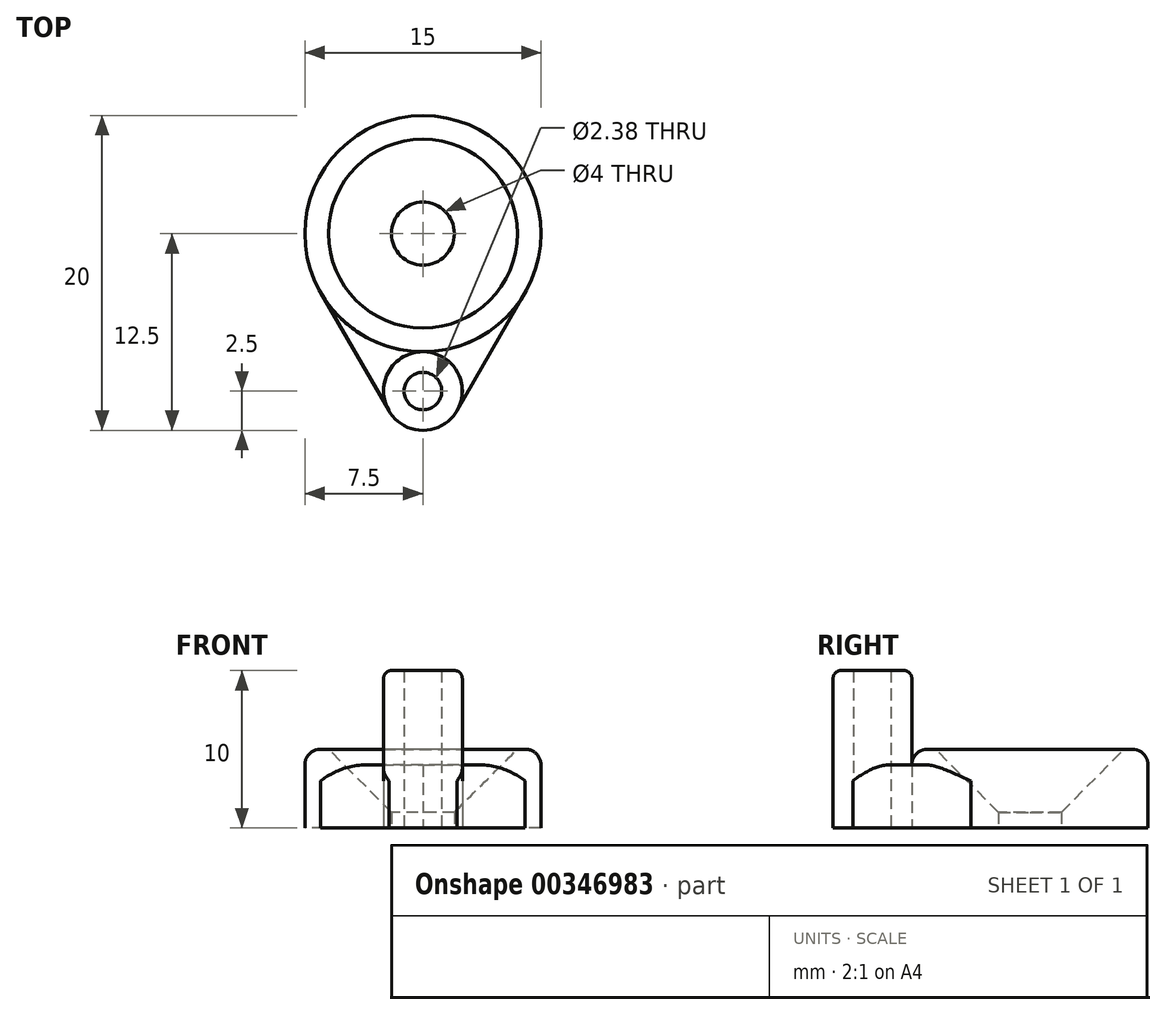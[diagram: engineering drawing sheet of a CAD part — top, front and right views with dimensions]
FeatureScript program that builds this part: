
annotation { "Feature Type Name" : "Feature", "Feature Type Description" : "" }
export const myFeature = defineFeature(function(context is Context, id is Id, definition is map)
    precondition{}
    {
        {
            var Q0;
            Q0=qCreatedBy(makeId("Top.planeOp"),FACE);
            var sketch = newSketch(context, id + "F0", { "sketchPlane" : qUnion([Q0])});
            skCircle(sketch, "E0", {"center": v(0, 0) * mm, "radius": 2.5 * mm});
            skCircle(sketch, "E1", {"center": v(0, 10) * mm, "radius": 7.5 * mm});
            skLineSegment(sketch, "E2", {"start": v(2.17, -1.25) * mm, "end": v(6.5, 6.25) * mm});
            skLineSegment(sketch, "E3", {"start": v(-2.17, -1.25) * mm, "end": v(-6.5, 6.25) * mm});
            skCircle(sketch, "E4", {"center": v(0, 0) * mm, "radius": 1.2 * mm});
            skCircle(sketch, "E5", {"center": v(0, 10) * mm, "radius": 2 * mm});
            skSolve(sketch);
        }
        {
            var Q0;
            Q0=makeQuery(id+"F0.imprint","IMPRINT",FACE,{"disambiguationData":[TD([[makeQuery(id+"F0.imprint","IMPRINT",EDGE,{"derivedFrom":sQuery(id+"F0.wireOp",EDGE,"E5")}),-1.0]])]});
            extrude(context, id + "F1", {"entities" : qUnion([Q0]), "depth" : 5 * mm});
        }
        {
            var Q0;
            Q0=makeQuery(id+"F0.imprint","IMPRINT",FACE,{"disambiguationData":[TD([[makeQuery(id+"F0.imprint","IMPRINT",EDGE,{"derivedFrom":sQuery(id+"F0.wireOp",EDGE,"E4")}),-1.0]])]});
            extrude(context, id + "F2", {"entities" : qUnion([Q0]), "depth" : 10 * mm});
        }
        {
            var Q0;
            {var subQ0=sQuery(id+"F0.wireOp",EDGE,"E2");Q0=makeQuery(id+"F0.imprint","IMPRINT",FACE,{"disambiguationData":[TD([[makeQuery(id+"F0.imprint","IMPRINT",EDGE,{"derivedFrom":subQ0}),1.0]])]});}
            var Q1;
            {var subQ0=sQuery(id+"F0.wireOp",EDGE,"E3");Q1=makeQuery(id+"F0.imprint","IMPRINT",FACE,{"disambiguationData":[TD([[makeQuery(id+"F0.imprint","IMPRINT",EDGE,{"derivedFrom":subQ0}),-1.0]])]});}
            extrude(context, id + "F3", {"entities" : qUnion([Q0, Q1]), "depth" : 4 * mm});
        }
        {
            var Q0;
            Q0=makeQuery(id+"F1.opExtrude","CAP_EDGE",EDGE,{"disambiguationData":[OSD([sQuery(id+"F0.wireOp",EDGE,"E1")])],"isStart":false});
            var Q1;
            Q1=makeQuery(id+"F3.opExtrude","CAP_EDGE",EDGE,{"disambiguationData":[OSD([sQuery(id+"F0.wireOp",EDGE,"E2")])],"isStart":false});
            var Q2;
            Q2=makeQuery(id+"F3.opExtrude","CAP_EDGE",EDGE,{"disambiguationData":[OSD([sQuery(id+"F0.wireOp",EDGE,"E3")])],"isStart":false});
            fillet(context, id + "F4", {"entities" : qUnion([Q0, Q1, Q2]), "radius" : 1 * mm, "tangentPropagation" : true, "allowEdgeOverflow" : false});
        }
        {
            var Q0;
            Q0=makeQuery(id+"F1.opExtrude","CAP_EDGE",EDGE,{"disambiguationData":[OSD([sQuery(id+"F0.wireOp",EDGE,"E5")])],"isStart":false});
            chamfer(context, id + "F5", {"entities" : qUnion([Q0]), "width" : 4 * mm, "tangentPropagation" : true});
        }
        {
            var Q0;
            Q0=makeQuery(id+"F2.opExtrude","CAP_EDGE",EDGE,{"disambiguationData":[OSD([sQuery(id+"F0.wireOp",EDGE,"E0")])],"isStart":false});
            fillet(context, id + "F6", {"entities" : qUnion([Q0]), "radius" : .5 * mm, "tangentPropagation" : true, "allowEdgeOverflow" : false});
        }
    });
